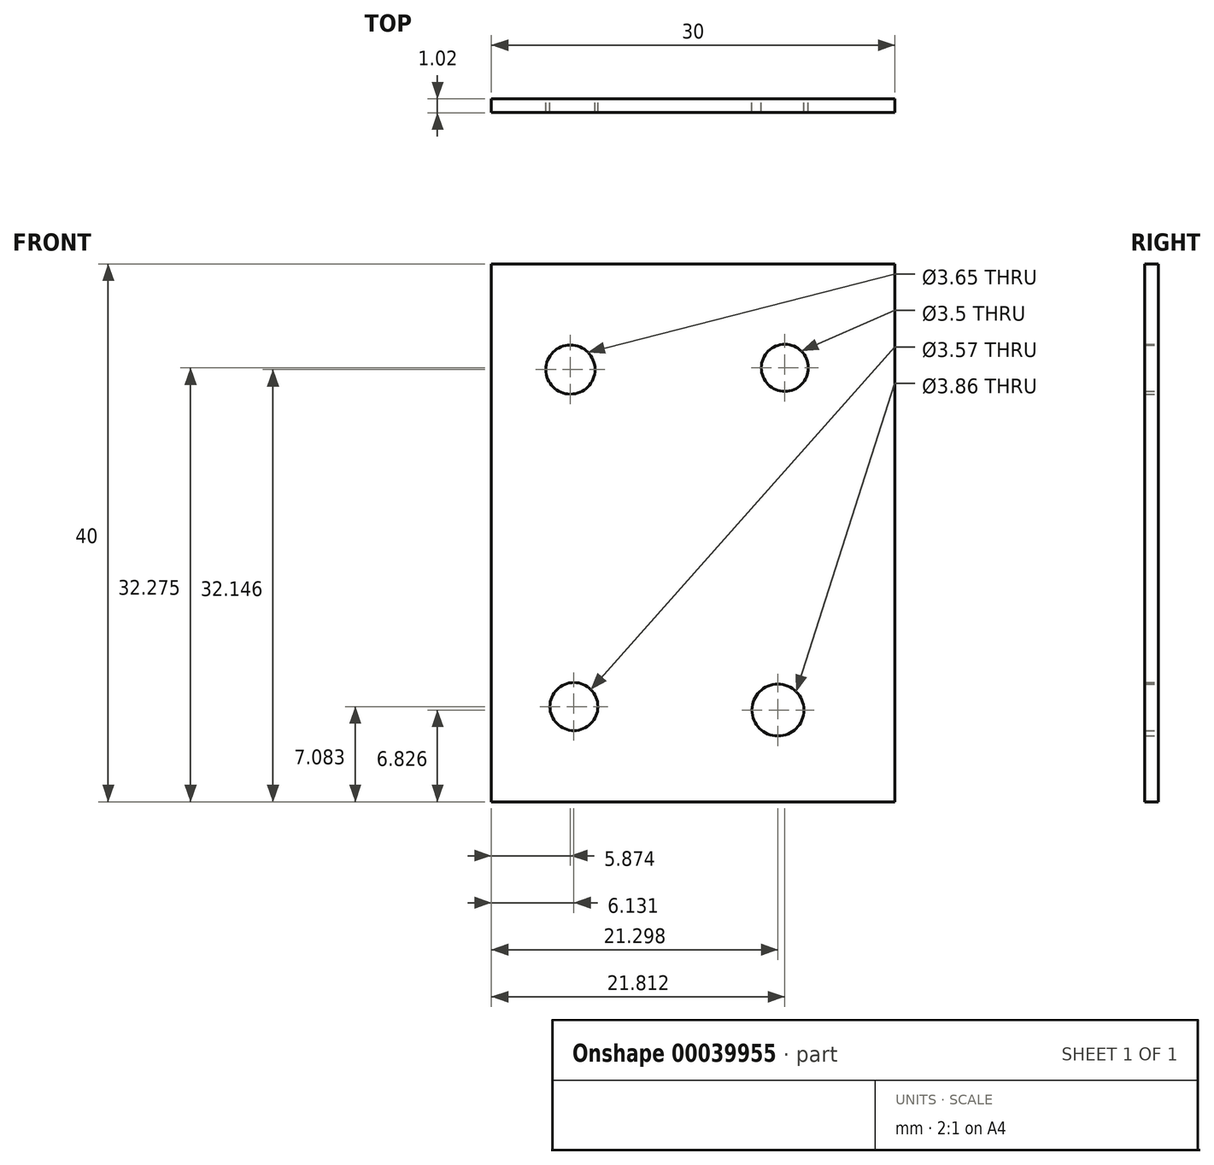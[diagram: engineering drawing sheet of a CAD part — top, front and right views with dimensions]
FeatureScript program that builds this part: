
annotation { "Feature Type Name" : "Feature", "Feature Type Description" : "" }
export const myFeature = defineFeature(function(context is Context, id is Id, definition is map)
    precondition{}
    {
        {
            var Q0;
            Q0=qCreatedBy(makeId("Front.planeOp"),FACE);
            var sketch = newSketch(context, id + "F0", { "sketchPlane" : qUnion([Q0])});
            skLineSegment(sketch, "E0.rect.bottom", {"start": v(15, -20) * mm, "end": v(-15, -20) * mm});
            skLineSegment(sketch, "E0.rect.top", {"start": v(15, 20) * mm, "end": v(-15, 20) * mm});
            skLineSegment(sketch, "E0.rect.left", {"start": v(15, -20) * mm, "end": v(15, 20) * mm});
            skLineSegment(sketch, "E0.rect.right", {"start": v(-15, -20) * mm, "end": v(-15, 20) * mm});
            skPoint(sketch, "E0.rect.middle", {"position": v(0, 0) * mm});
            skCircle(sketch, "E1", {"center": v(-9.13, 12.15) * mm, "radius": 1.83 * mm});
            skCircle(sketch, "E2", {"center": v(6.81, 12.27) * mm, "radius": 1.75 * mm});
            skCircle(sketch, "E3", {"center": v(-8.87, -12.92) * mm, "radius": 1.79 * mm});
            skCircle(sketch, "E4", {"center": v(6.3, -13.17) * mm, "radius": 1.93 * mm});
            skSolve(sketch);
        }
        {
            var Q0;
            Q0 = qSketchRegion(id + "F0", true);
            extrude(context, id + "F1", {"entities" : qUnion([Q0]), "depth" : 1.02 * mm});
        }
    });
